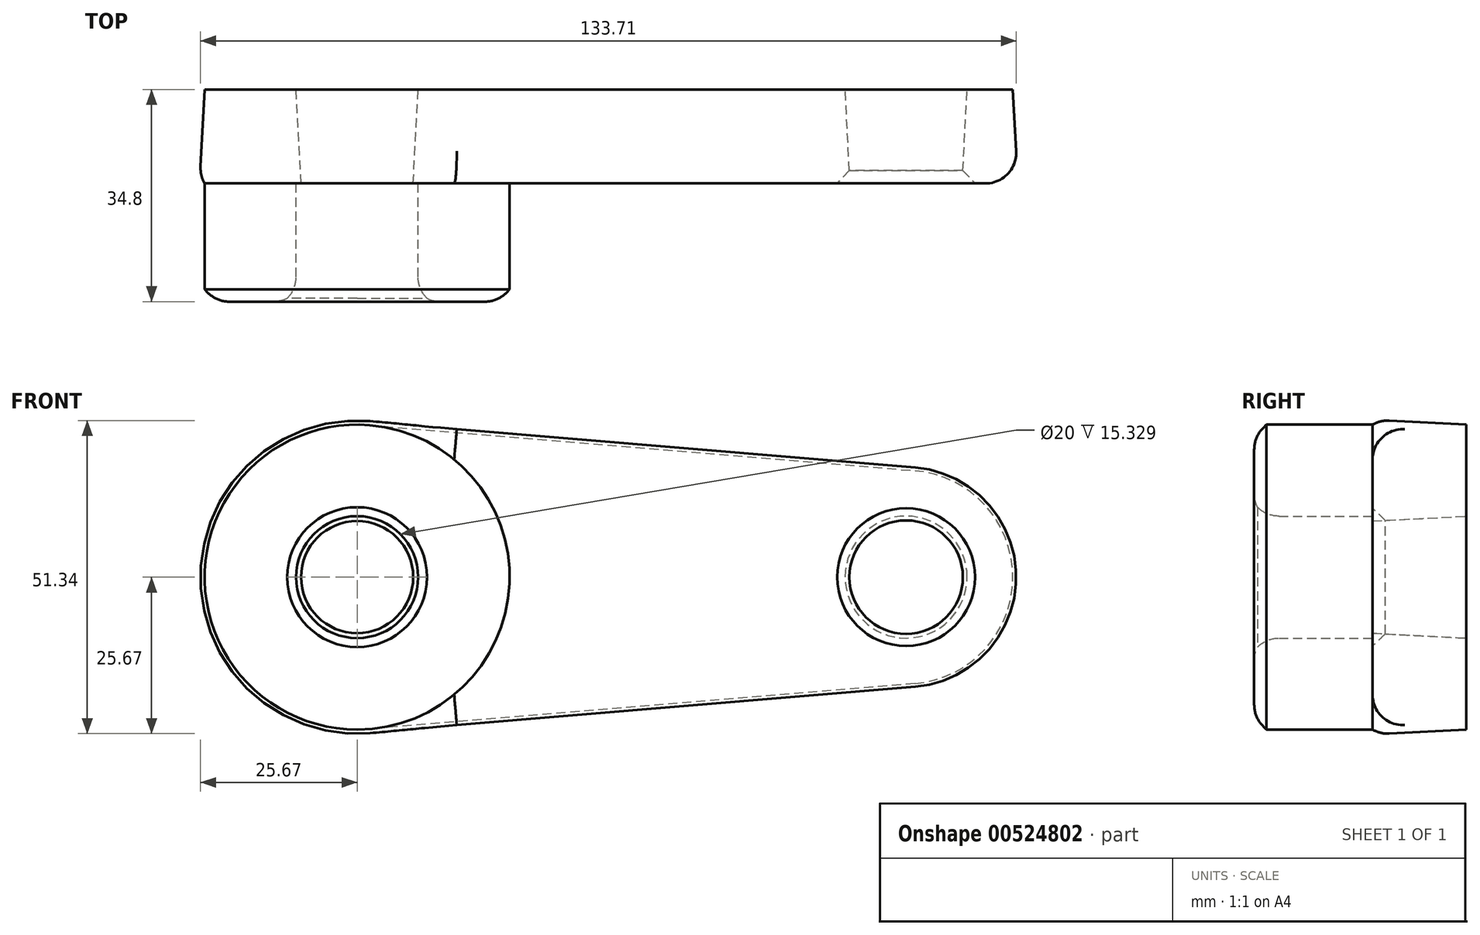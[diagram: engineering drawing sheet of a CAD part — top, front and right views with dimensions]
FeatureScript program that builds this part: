
annotation { "Feature Type Name" : "Feature", "Feature Type Description" : "" }
export const myFeature = defineFeature(function(context is Context, id is Id, definition is map)
    precondition{}
    {
        {
            var Q0;
            Q0=qCreatedBy(makeId("Front.planeOp"),FACE);
            var sketch = newSketch(context, id + "F0", { "sketchPlane" : qUnion([Q0])});
            skCircle(sketch, "E0", {"center": v(0, 0) * mm, "radius": 25 * mm});
            skCircle(sketch, "E1", {"center": v(90, 0) * mm, "radius": 17.5 * mm});
            skLineSegment(sketch, "E2", {"start": v(2.08, 24.91) * mm, "end": v(91.46, 17.44) * mm});
            skLineSegment(sketch, "E3", {"start": v(2.08, -24.91) * mm, "end": v(91.46, -17.44) * mm});
            skCircle(sketch, "E4", {"center": v(0, 0) * mm, "radius": 10 * mm});
            skCircle(sketch, "E5", {"center": v(90, 0) * mm, "radius": 10 * mm});
            skSolve(sketch);
        }
        {
            var Q0;
            Q0=qSketchRegion(id+"F0",true);
            extrude(context, id + "F1", {"entities" : qUnion([Q0]), "depth" : 15.4 * mm, "hasDraft" : true, "draftAngle" : 3 * degree, "offsetDistance" : 25 * mm});
        }
        {
            var Q0;
            Q0=makeQuery(id+"F0.imprint","IMPRINT",FACE,{"disambiguationData":[TD([[makeQuery(id+"F0.imprint","IMPRINT",EDGE,{"derivedFrom":sQuery(id+"F0.wireOp",EDGE,"E4")}),-1.0]])]});
            extrude(context, id + "F2", {"entities" : qUnion([Q0]), "operationType" : NewBodyOperationType.ADD, "depth" : 34.8 * mm, "offsetDistance" : 25 * mm});
        }
        {
            var Q0;
            Q0=makeQuery(id+"F2.opExtrude","CAP_EDGE",EDGE,{"disambiguationData":[OSD([sQuery(id+"F0.wireOp",EDGE,"E0")])],"isStart":false});
            var Q1;
            Q1=makeQuery(id+"F2.opExtrude","CAP_EDGE",EDGE,{"disambiguationData":[OSD([sQuery(id+"F0.wireOp",EDGE,"E4")])],"isStart":false});
            var Q2;
            Q2=makeQuery(id+"F1.opExtrude","CAP_EDGE",EDGE,{"disambiguationData":[OSD([sQuery(id+"F0.wireOp",EDGE,"E5")])],"isStart":false});
            chamfer(context, id + "F3", {"entities" : qUnion([Q0, Q1, Q2]), "width" : 2 * mm, "tangentPropagation" : true});
        }
        {
            var Q0;
            Q0=makeQuery(id+"F1.opExtrude","CAP_EDGE",EDGE,{"disambiguationData":[OSD([sQuery(id+"F0.wireOp",EDGE,"E2")])],"isStart":false});
            var Q1;
            Q1=makeQuery(id+"F1.opExtrude","CAP_EDGE",EDGE,{"disambiguationData":[OSD([sQuery(id+"F0.wireOp",EDGE,"E1")])],"isStart":false});
            fillet(context, id + "F4", {"entities" : qUnion([Q0, Q1]), "radius" : 5 * mm, "tangentPropagation" : true, "allowEdgeOverflow" : false});
        }
        {
            var Q0;
            {var subQ0=sQuery(id+"F0.wireOp",EDGE,"E0");Q0=makeQuery(id+"F3.opChamfer","BLEND_EDGE",EDGE,{"blendedFrom":[makeQuery(id+"F2.opExtrude","CAP_EDGE",EDGE,{"disambiguationData":[OSD([subQ0])],"isStart":false}),makeQuery(id+"F2.opExtrude","CAP_FACE",FACE,{"disambiguationData":[OSD([subQ0,sQuery(id+"F0.wireOp",EDGE,"E4")])],"isStart":false})],"blendedInto":[makeQuery(id+"F2.opExtrude","CAP_FACE",FACE,{"disambiguationData":[OSD([subQ0,sQuery(id+"F0.wireOp",EDGE,"E4")])],"isStart":false})]});}
            var Q1;
            {var subQ0=sQuery(id+"F0.wireOp",EDGE,"E4");Q1=makeQuery(id+"F3.opChamfer","BLEND_EDGE",EDGE,{"blendedFrom":[makeQuery(id+"F2.opExtrude","CAP_EDGE",EDGE,{"disambiguationData":[OSD([subQ0])],"isStart":false}),makeQuery(id+"F2.boolean.opBoolean","MERGE",FACE,{"derivedFrom":[makeQuery(id+"F1.opExtrude","SWEPT_FACE",FACE,{"disambiguationData":[OSD([subQ0])]}),makeQuery(id+"F2.opExtrude","SWEPT_FACE",FACE,{"disambiguationData":[OSD([subQ0])]})]})],"blendedInto":[makeQuery(id+"F2.boolean.opBoolean","MERGE",FACE,{"derivedFrom":[makeQuery(id+"F1.opExtrude","SWEPT_FACE",FACE,{"disambiguationData":[OSD([subQ0])]}),makeQuery(id+"F2.opExtrude","SWEPT_FACE",FACE,{"disambiguationData":[OSD([subQ0])]})]})]});}
            fillet(context, id + "F5", {"entities" : qUnion([Q0, Q1]), "radius" : 5 * mm, "tangentPropagation" : true, "allowEdgeOverflow" : false});
        }
        {
            var Q0;
            {var subQ0=sQuery(id+"F0.wireOp",EDGE,"E4");Q0=makeQuery(id+"F3.opChamfer","BLEND_EDGE",EDGE,{"blendedFrom":[makeQuery(id+"F2.opExtrude","CAP_EDGE",EDGE,{"disambiguationData":[OSD([subQ0])],"isStart":false}),makeQuery(id+"F2.opExtrude","CAP_FACE",FACE,{"disambiguationData":[OSD([sQuery(id+"F0.wireOp",EDGE,"E0"),subQ0])],"isStart":false})],"blendedInto":[makeQuery(id+"F2.opExtrude","CAP_FACE",FACE,{"disambiguationData":[OSD([sQuery(id+"F0.wireOp",EDGE,"E0"),subQ0])],"isStart":false})]});}
            fillet(context, id + "F6", {"entities" : qUnion([Q0]), "radius" : 5 * mm, "tangentPropagation" : true, "allowEdgeOverflow" : false});
        }
    });
